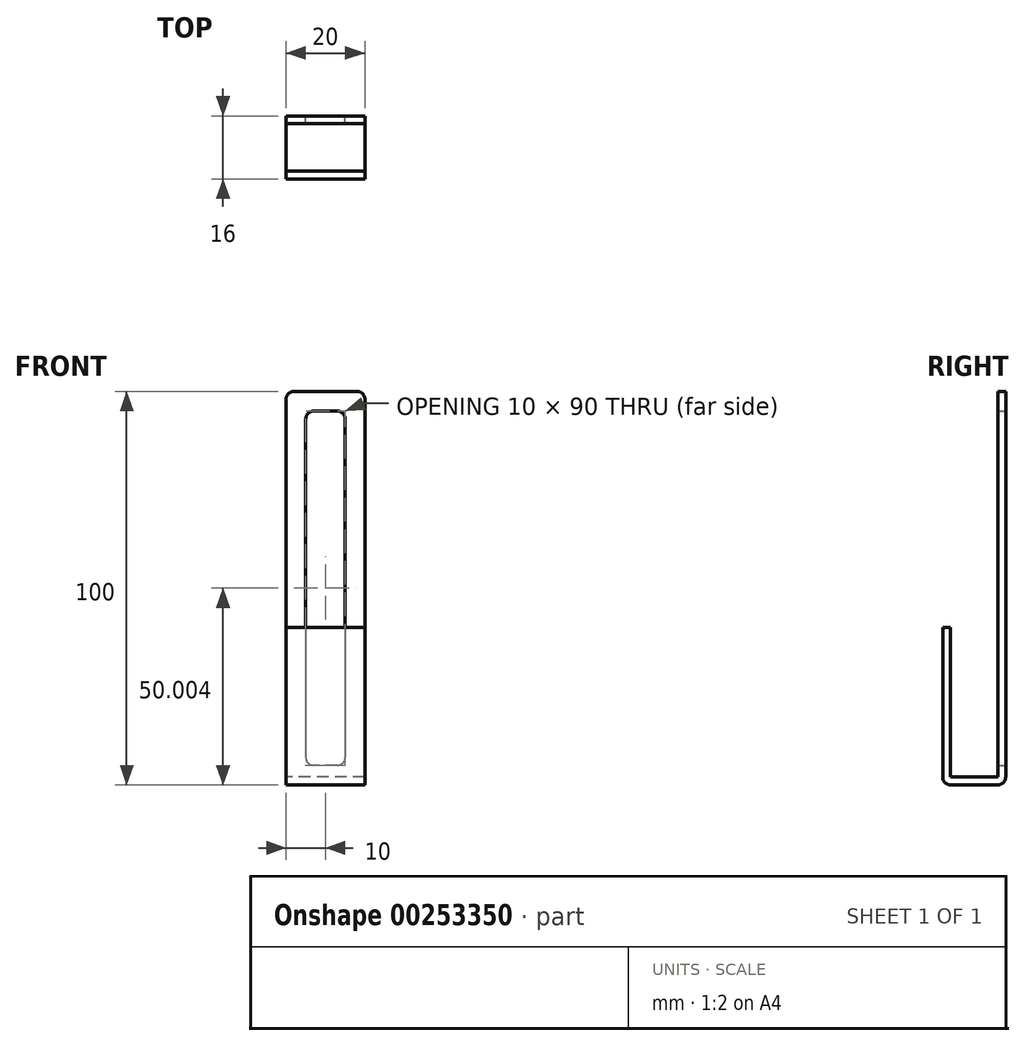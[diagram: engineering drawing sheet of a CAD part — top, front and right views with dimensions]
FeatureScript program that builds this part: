
annotation { "Feature Type Name" : "Feature", "Feature Type Description" : "" }
export const myFeature = defineFeature(function(context is Context, id is Id, definition is map)
    precondition{}
    {
        {
            var Q0;
            Q0=qCreatedBy(makeId("Right.planeOp"),FACE);
            var sketch = newSketch(context, id + "F0", { "sketchPlane" : qUnion([Q0])});
            skLineSegment(sketch, "E0.bottom", {"start": v(-10.13, 59.47) * mm, "end": v(-0.13, 59.47) * mm});
            skLineSegment(sketch, "E0.top", {"start": v(-16.13, -40.53) * mm, "end": v(-0.13, -40.53) * mm});
            skLineSegment(sketch, "E0.left", {"start": v(-16.13, -0.53) * mm, "end": v(-16.13, -40.53) * mm});
            skLineSegment(sketch, "E0.right", {"start": v(-0.13, 59.47) * mm, "end": v(-0.13, -40.53) * mm});
            skLineSegment(sketch, "E1", {"start": v(-10.13, 59.47) * mm, "end": v(-10.13, -0.53) * mm});
            skLineSegment(sketch, "E2", {"start": v(-10.13, -0.53) * mm, "end": v(-16.13, -0.53) * mm});
            skSolve(sketch);
        }
        {
            var Q0;
            Q0=makeQuery(id+"F0.imprint","IMPRINT",FACE,{"disambiguationData":[TD([[makeQuery(id+"F0.imprint","IMPRINT",EDGE,{"derivedFrom":sQuery(id+"F0.wireOp",EDGE,"E0.bottom")}),-1.0]])]});
            var Q1;
            Q1=sQuery(id+"F0.wireOp",EDGE,"E1");
            var Q2;
            Q2=sQuery(id+"F0.wireOp",EDGE,"E0.right");
            var Q3;
            Q3=sQuery(id+"F0.wireOp",EDGE,"E0.left");
            var Q4;
            Q4=sQuery(id+"F0.wireOp",EDGE,"E0.top");
            var Q5;
            Q5=sQuery(id+"F0.wireOp",EDGE,"E0.bottom");
            var Q6;
            Q6=sQuery(id+"F0.wireOp",EDGE,"E2");
            extrude(context, id + "F1", {"entities" : qUnion([Q0]), "surfaceEntities" : qUnion([Q1, Q2, Q3, Q4, Q5, Q6]), "endBound" : BoundingType.SYMMETRIC, "depth" : 20 * mm});
        }
        {
            var Q0;
            Q0=makeQuery(id+"F1.opExtrude","SWEPT_FACE",FACE,{"disambiguationData":[OSD([sQuery(id+"F0.wireOp",EDGE,"E2")])]});
            var Q1;
            Q1=makeQuery(id+"F1.opExtrude","SWEPT_FACE",FACE,{"disambiguationData":[OSD([sQuery(id+"F0.wireOp",EDGE,"E1")])]});
            var Q2;
            Q2=makeQuery(id+"F1.opExtrude","SWEPT_FACE",FACE,{"disambiguationData":[OSD([sQuery(id+"F0.wireOp",EDGE,"E0.bottom")])]});
            var Q3;
            Q3=makeQuery(id+"F1.opExtrude","CAP_FACE",FACE,{"disambiguationData":[OSD([sQuery(id+"F0.wireOp",EDGE,"E0.bottom"),sQuery(id+"F0.wireOp",EDGE,"E0.top"),sQuery(id+"F0.wireOp",EDGE,"E0.left"),sQuery(id+"F0.wireOp",EDGE,"E0.right"),sQuery(id+"F0.wireOp",EDGE,"E1"),sQuery(id+"F0.wireOp",EDGE,"E2")])],"isStart":false});
            var Q4;
            Q4=makeQuery(id+"F1.opExtrude","CAP_FACE",FACE,{"disambiguationData":[OSD([sQuery(id+"F0.wireOp",EDGE,"E0.bottom"),sQuery(id+"F0.wireOp",EDGE,"E0.top"),sQuery(id+"F0.wireOp",EDGE,"E0.left"),sQuery(id+"F0.wireOp",EDGE,"E0.right"),sQuery(id+"F0.wireOp",EDGE,"E1"),sQuery(id+"F0.wireOp",EDGE,"E2")])],"isStart":true});
            shell(context, id + "F2", {"entities" : qUnion([Q0, Q1, Q2, Q3, Q4]), "thickness" : 2 * mm});
        }
        {
            var Q0;
            Q0=makeQuery(id+"F1.opExtrude","SWEPT_FACE",FACE,{"disambiguationData":[OSD([sQuery(id+"F0.wireOp",EDGE,"E0.right")])]});
            var sketch = newSketch(context, id + "F3", { "sketchPlane" : qUnion([Q0])});
            skLineSegment(sketch, "E3.bottom", {"start": v(-5, 54.47) * mm, "end": v(5, 54.47) * mm});
            skLineSegment(sketch, "E3.top", {"start": v(-5, -35.53) * mm, "end": v(5, -35.53) * mm});
            skLineSegment(sketch, "E3.left", {"start": v(-5, 54.47) * mm, "end": v(-5, -35.53) * mm});
            skLineSegment(sketch, "E3.right", {"start": v(5, 54.47) * mm, "end": v(5, -35.53) * mm});
            skSolve(sketch);
        }
        {
            var Q0;
            Q0=makeQuery(id+"F3.imprint","IMPRINT",FACE,{"disambiguationData":[TD([[makeQuery(id+"F3.imprint","IMPRINT",EDGE,{"derivedFrom":sQuery(id+"F3.wireOp",EDGE,"E3.bottom")}),-1.0]])]});
            extrude(context, id + "F4", {"entities" : qUnion([Q0]), "operationType" : NewBodyOperationType.REMOVE, "oppositeDirection" : true, "depth" : 2 * mm});
        }
        {
            var Q0;
            Q0=makeQuery(id+"F1.opExtrude","CAP_EDGE",EDGE,{"disambiguationData":[OSD([sQuery(id+"F0.wireOp",EDGE,"E0.bottom")])],"isStart":false});
            var Q1;
            Q1=makeQuery(id+"F1.opExtrude","CAP_EDGE",EDGE,{"disambiguationData":[OSD([sQuery(id+"F0.wireOp",EDGE,"E0.bottom")])],"isStart":true});
            var Q2;
            Q2=makeQuery(id+"F4.boolean.opBoolean","COPY",EDGE,{"derivedFrom":makeQuery(id+"F4.opExtrude","SWEPT_EDGE",EDGE,{"disambiguationData":[OSD([sQuery(id+"F3.wireOp",EDGE,"E3.bottom"),sQuery(id+"F3.wireOp",EDGE,"E3.right")])]})});
            var Q3;
            Q3=makeQuery(id+"F4.boolean.opBoolean","COPY",EDGE,{"derivedFrom":makeQuery(id+"F4.opExtrude","SWEPT_EDGE",EDGE,{"disambiguationData":[OSD([sQuery(id+"F3.wireOp",EDGE,"E3.bottom"),sQuery(id+"F3.wireOp",EDGE,"E3.left")])]})});
            var Q4;
            Q4=makeQuery(id+"F1.opExtrude","SWEPT_EDGE",EDGE,{"disambiguationData":[OSD([sQuery(id+"F0.wireOp",EDGE,"E0.top"),sQuery(id+"F0.wireOp",EDGE,"E0.right")])]});
            var Q5;
            Q5=makeQuery(id+"F1.opExtrude","SWEPT_EDGE",EDGE,{"disambiguationData":[OSD([sQuery(id+"F0.wireOp",EDGE,"E0.top"),sQuery(id+"F0.wireOp",EDGE,"E0.left")])]});
            var Q6;
            Q6=makeQuery(id+"F4.boolean.opBoolean","COPY",EDGE,{"derivedFrom":makeQuery(id+"F4.opExtrude","SWEPT_EDGE",EDGE,{"disambiguationData":[OSD([sQuery(id+"F3.wireOp",EDGE,"E3.top"),sQuery(id+"F3.wireOp",EDGE,"E3.right")])]})});
            var Q7;
            Q7=makeQuery(id+"F4.boolean.opBoolean","COPY",EDGE,{"derivedFrom":makeQuery(id+"F4.opExtrude","SWEPT_EDGE",EDGE,{"disambiguationData":[OSD([sQuery(id+"F3.wireOp",EDGE,"E3.top"),sQuery(id+"F3.wireOp",EDGE,"E3.left")])]})});
            fillet(context, id + "F5", {"entities" : qUnion([Q0, Q1, Q2, Q3, Q4, Q5, Q6, Q7]), "radius" : 2 * mm, "allowEdgeOverflow" : false});
        }
    });
